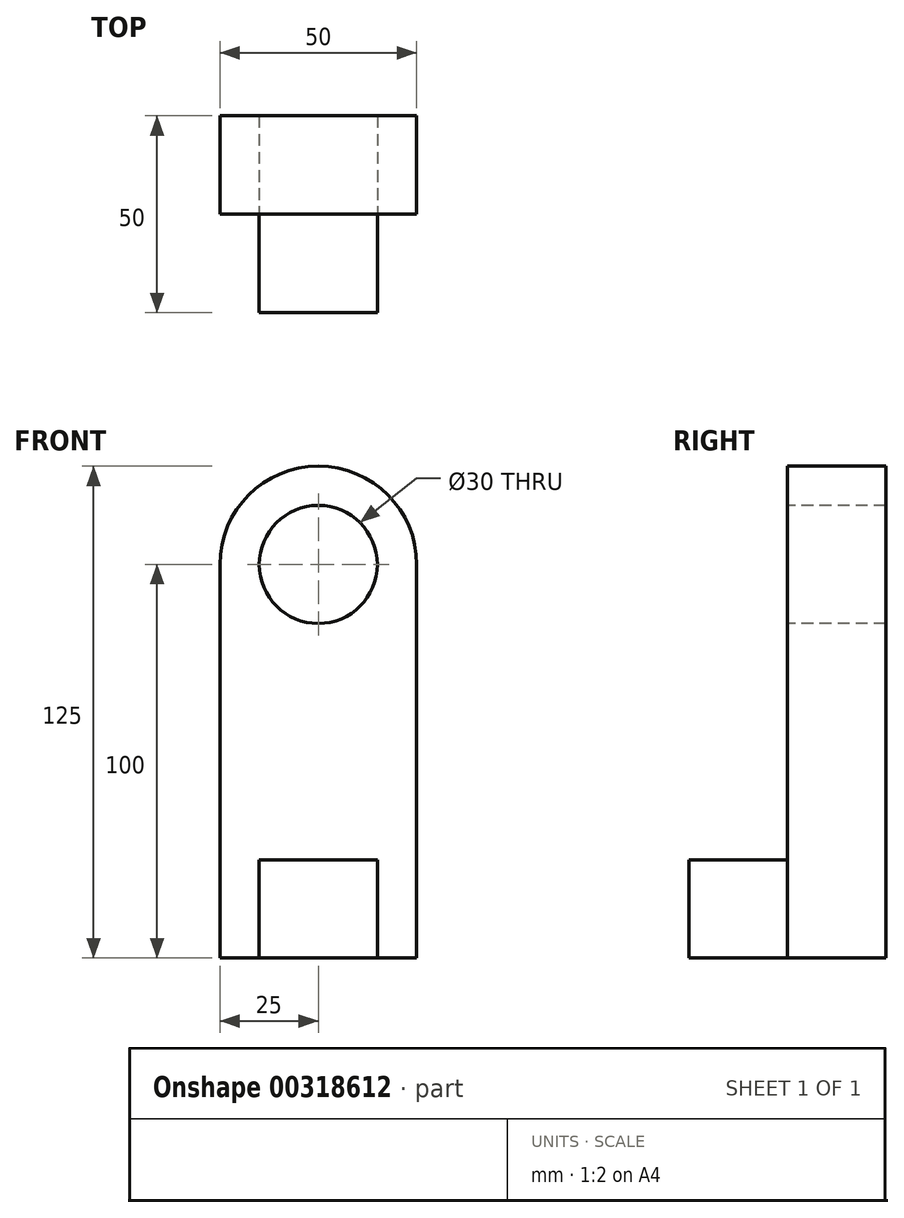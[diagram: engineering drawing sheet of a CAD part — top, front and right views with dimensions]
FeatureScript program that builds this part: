
annotation { "Feature Type Name" : "Feature", "Feature Type Description" : "" }
export const myFeature = defineFeature(function(context is Context, id is Id, definition is map)
    precondition{}
    {
        {
            var Q0;
            Q0=qCreatedBy(makeId("Top.planeOp"),FACE);
            var sketch = newSketch(context, id + "F0", { "sketchPlane" : qUnion([Q0])});
            skLineSegment(sketch, "E0.bottom", {"start": v(0, 0) * mm, "end": v(-30, 0) * mm});
            skLineSegment(sketch, "E0.top", {"start": v(0, -50) * mm, "end": v(-30, -50) * mm});
            skLineSegment(sketch, "E0.left", {"start": v(0, 0) * mm, "end": v(0, -50) * mm});
            skLineSegment(sketch, "E0.right", {"start": v(-30, 0) * mm, "end": v(-30, -50) * mm});
            skSolve(sketch);
        }
        {
            var Q0;
            Q0=makeQuery(id+"F0.imprint","IMPRINT",FACE,{"disambiguationData":[TD([[makeQuery(id+"F0.imprint","IMPRINT",EDGE,{"derivedFrom":sQuery(id+"F0.wireOp",EDGE,"E0.bottom")}),1.0]])]});
            extrude(context, id + "F1", {"entities" : qUnion([Q0]), "depth" : 25 * mm});
        }
        {
            var Q0;
            Q0=makeQuery(id+"F1.opExtrude","SWEPT_FACE",FACE,{"disambiguationData":[OSD([sQuery(id+"F0.wireOp",EDGE,"E0.bottom")])]});
            var sketch = newSketch(context, id + "F2", { "sketchPlane" : qUnion([Q0])});
            skLineSegment(sketch, "E1", {"start": v(15, 0) * mm, "end": v(15, 25) * mm, "construction": true});
            skLineSegment(sketch, "E2.bottom", {"start": v(-10, 0) * mm, "end": v(40, 0) * mm});
            skLineSegment(sketch, "E2.top", {"start": v(-10, 100) * mm, "end": v(40, 100) * mm, "construction": true});
            skLineSegment(sketch, "E2.left", {"start": v(-10, 0) * mm, "end": v(-10, 100) * mm});
            skLineSegment(sketch, "E2.right", {"start": v(40, 0) * mm, "end": v(40, 100) * mm});
            skArc(sketch, "E3", {"start": v(40, 100) * mm, "mid": v(15, 125) * mm, "end": v(-10, 100) * mm});
            skSolve(sketch);
        }
        {
            var Q0;
            {var subQ7=sQuery(id+"F2.wireOp",EDGE,"E3");var subQ9=sQuery(id+"F2.wireOp",EDGE,"E2.bottom");Q0=qUnion([makeQuery(id+"F2.imprint","IMPRINT",FACE,{"disambiguationData":[TD([[makeQuery(id+"F2.imprint","IMPRINT",EDGE,{"derivedFrom":subQ7}),1.0]])]}),makeQuery(id+"F2.imprint","IMPRINT",FACE,{"disambiguationData":[TD([[makeQuery(id+"F2.imprint","IMPRINT",EDGE,{"derivedFrom":subQ9}),1.0]])]})]);}
            extrude(context, id + "F3", {"entities" : qUnion([Q0]), "operationType" : NewBodyOperationType.ADD, "oppositeDirection" : true, "depth" : 25 * mm});
        }
        {
            var Q0;
            Q0=makeQuery(id+"F3.opExtrude","CAP_FACE",FACE,{"disambiguationData":[OSD([sQuery(id+"F2.wireOp",EDGE,"E2.bottom"),sQuery(id+"F2.wireOp",EDGE,"E2.left"),sQuery(id+"F2.wireOp",EDGE,"E2.right"),sQuery(id+"F2.wireOp",EDGE,"E3")])],"isStart":false});
            var sketch = newSketch(context, id + "F4", { "sketchPlane" : qUnion([Q0])});
            skCircle(sketch, "E4", {"center": v(-15, 100) * mm, "radius": 15 * mm});
            skSolve(sketch);
        }
        {
            var Q0;
            Q0=makeQuery(id+"F4.imprint","IMPRINT",FACE,{"disambiguationData":[TD([[makeQuery(id+"F4.imprint","IMPRINT",EDGE,{"derivedFrom":sQuery(id+"F4.wireOp",EDGE,"E4")}),1.0]])]});
            extrude(context, id + "F5", {"entities" : qUnion([Q0]), "operationType" : NewBodyOperationType.REMOVE, "oppositeDirection" : true, "depth" : 25 * mm});
        }
    });
